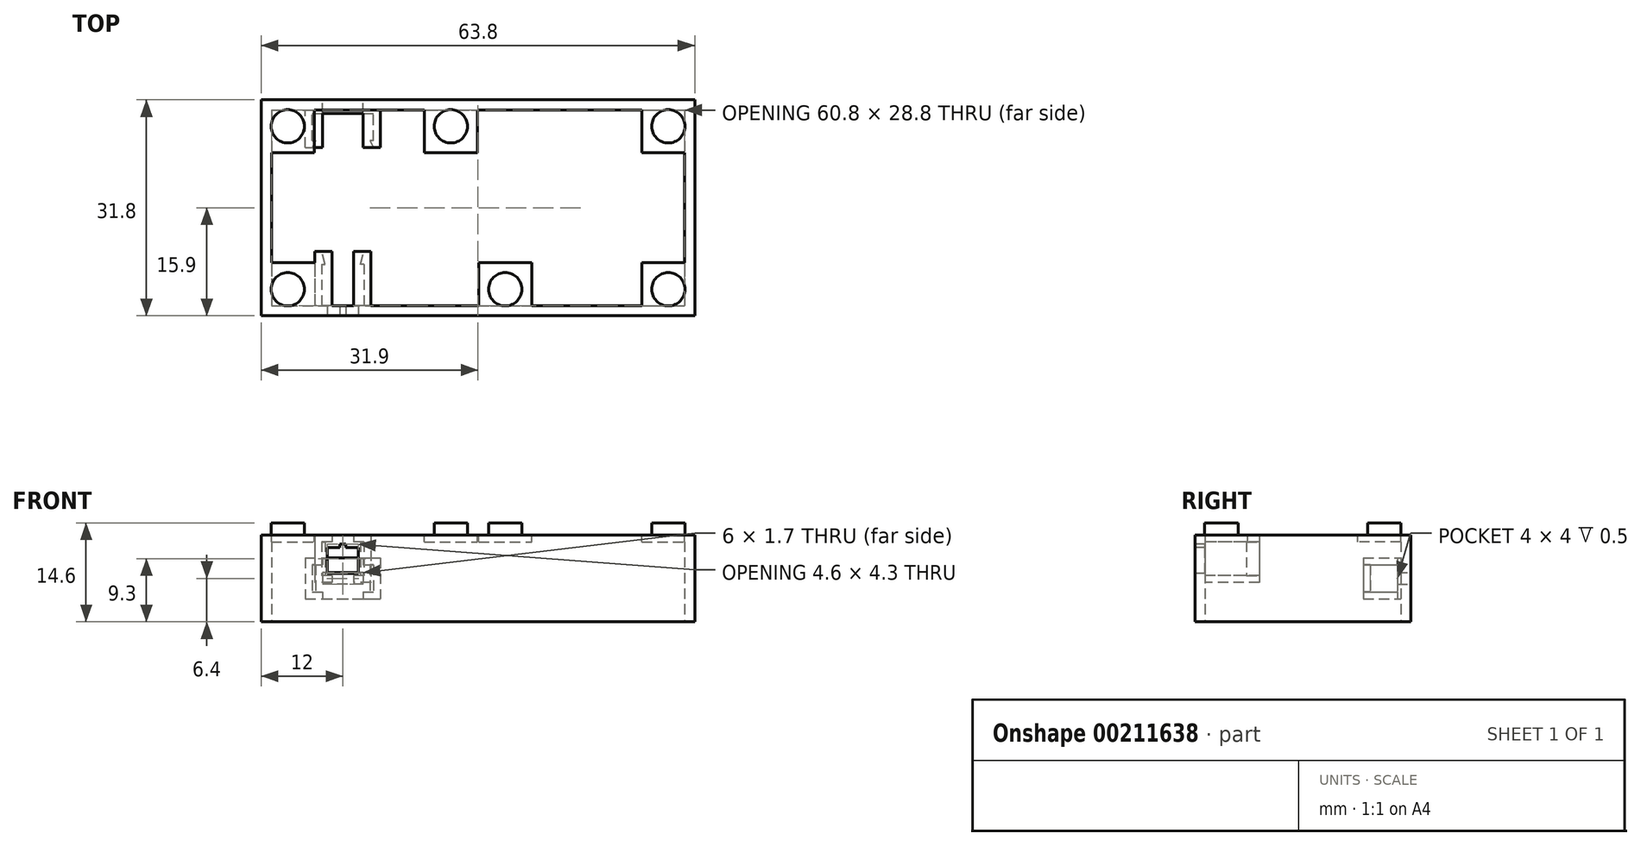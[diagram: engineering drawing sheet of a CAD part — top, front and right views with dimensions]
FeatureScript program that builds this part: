
annotation { "Feature Type Name" : "Feature", "Feature Type Description" : "" }
export const myFeature = defineFeature(function(context is Context, id is Id, definition is map)
    precondition{}
    {
        {
            var Q0;
            Q0=qCreatedBy(makeId("Top.planeOp"),FACE);
            var sketch = newSketch(context, id + "F0", { "sketchPlane" : qUnion([Q0])});
            skLineSegment(sketch, "E0.bottom", {"start": v(0, 31.8) * mm, "end": v(63.8, 31.8) * mm});
            skLineSegment(sketch, "E0.top", {"start": v(0, 0) * mm, "end": v(63.8, 0) * mm});
            skLineSegment(sketch, "E0.left", {"start": v(0, 31.8) * mm, "end": v(0, 0) * mm});
            skLineSegment(sketch, "E0.right", {"start": v(63.8, 31.8) * mm, "end": v(63.8, 0) * mm});
            skPoint(sketch, "E1", {"position": v(31.9, 31.8) * mm});
            skPoint(sketch, "E2", {"position": v(0, 15.9) * mm});
            skLineSegment(sketch, "E3.0", {"start": v(1.5, 30.3) * mm, "end": v(1.5, 1.5) * mm});
            skLineSegment(sketch, "E3.1", {"start": v(1.5, 30.3) * mm, "end": v(62.3, 30.3) * mm});
            skLineSegment(sketch, "E3.2", {"start": v(62.3, 30.3) * mm, "end": v(62.3, 1.5) * mm});
            skLineSegment(sketch, "E3.3", {"start": v(1.5, 1.5) * mm, "end": v(62.3, 1.5) * mm});
            skSolve(sketch);
        }
        {
            var Q0;
            Q0=qSketchRegion(id+"F0",true);
            extrude(context, id + "F1", {"entities" : qUnion([Q0]), "depth" : 12.8 * mm});
        }
        {
            var Q0;
            Q0=makeQuery(id+"F1.opExtrude","CAP_FACE",FACE,{"disambiguationData":[OSD([sQuery(id+"F0.wireOp",EDGE,"E0.bottom"),sQuery(id+"F0.wireOp",EDGE,"E0.top"),sQuery(id+"F0.wireOp",EDGE,"E0.left"),sQuery(id+"F0.wireOp",EDGE,"E0.right"),sQuery(id+"F0.wireOp",EDGE,"E3.0"),sQuery(id+"F0.wireOp",EDGE,"E3.1"),sQuery(id+"F0.wireOp",EDGE,"E3.2"),sQuery(id+"F0.wireOp",EDGE,"E3.3")])],"isStart":false});
            var sketch = newSketch(context, id + "F2", { "sketchPlane" : qUnion([Q0])});
            skLineSegment(sketch, "E4.bottom", {"start": v(0, 31.8) * mm, "end": v(7.8, 31.8) * mm});
            skLineSegment(sketch, "E4.top", {"start": v(0, 24) * mm, "end": v(7.8, 24) * mm});
            skLineSegment(sketch, "E4.left", {"start": v(0, 31.8) * mm, "end": v(0, 24) * mm});
            skLineSegment(sketch, "E4.right", {"start": v(7.8, 31.8) * mm, "end": v(7.8, 24) * mm});
            skLineSegment(sketch, "E5.bottom", {"start": v(0, 0) * mm, "end": v(7.8, 0) * mm});
            skLineSegment(sketch, "E5.top", {"start": v(0, 7.8) * mm, "end": v(7.8, 7.8) * mm});
            skLineSegment(sketch, "E5.left", {"start": v(0, 0) * mm, "end": v(0, 7.8) * mm});
            skLineSegment(sketch, "E5.right", {"start": v(7.8, 0) * mm, "end": v(7.8, 7.8) * mm});
            skLineSegment(sketch, "E6.bottom", {"start": v(63.8, 31.8) * mm, "end": v(56, 31.8) * mm});
            skLineSegment(sketch, "E6.top", {"start": v(63.8, 24) * mm, "end": v(56, 24) * mm});
            skLineSegment(sketch, "E6.left", {"start": v(63.8, 31.8) * mm, "end": v(63.8, 24) * mm});
            skLineSegment(sketch, "E6.right", {"start": v(56, 31.8) * mm, "end": v(56, 24) * mm});
            skLineSegment(sketch, "E7.bottom", {"start": v(63.8, 0) * mm, "end": v(56, 0) * mm});
            skLineSegment(sketch, "E7.top", {"start": v(63.8, 7.8) * mm, "end": v(56, 7.8) * mm});
            skLineSegment(sketch, "E7.left", {"start": v(63.8, 0) * mm, "end": v(63.8, 7.8) * mm});
            skLineSegment(sketch, "E7.right", {"start": v(56, 0) * mm, "end": v(56, 7.8) * mm});
            skPoint(sketch, "E8.centerSnap0", {"position": v(3.9, 24) * mm});
            skPoint(sketch, "E8.centerSnap1", {"position": v(0, 27.9) * mm});
            skPoint(sketch, "E9.centerSnap0", {"position": v(3.9, 0) * mm});
            skPoint(sketch, "E9.centerSnap1", {"position": v(0, 3.9) * mm});
            skPoint(sketch, "E10.centerSnap0", {"position": v(63.8, 27.9) * mm});
            skPoint(sketch, "E10.centerSnap1", {"position": v(59.9, 31.8) * mm});
            skPoint(sketch, "E11.centerSnap0", {"position": v(59.9, 0) * mm});
            skPoint(sketch, "E11.centerSnap1", {"position": v(63.8, 3.9) * mm});
            skLineSegment(sketch, "E12.bottom", {"start": v(24, 31.8) * mm, "end": v(31.8, 31.8) * mm});
            skLineSegment(sketch, "E12.top", {"start": v(24, 24) * mm, "end": v(31.8, 24) * mm});
            skLineSegment(sketch, "E12.left", {"start": v(24, 31.8) * mm, "end": v(24, 24) * mm});
            skLineSegment(sketch, "E12.right", {"start": v(31.8, 31.8) * mm, "end": v(31.8, 24) * mm});
            skLineSegment(sketch, "E13.bottom", {"start": v(39.8, 0) * mm, "end": v(32, 0) * mm});
            skLineSegment(sketch, "E13.top", {"start": v(39.8, 7.8) * mm, "end": v(32, 7.8) * mm});
            skLineSegment(sketch, "E13.left", {"start": v(39.8, 0) * mm, "end": v(39.8, 7.8) * mm});
            skLineSegment(sketch, "E13.right", {"start": v(32, 0) * mm, "end": v(32, 7.8) * mm});
            skPoint(sketch, "E14", {"position": v(27.9, 31.8) * mm});
            skPoint(sketch, "E15", {"position": v(35.9, 0) * mm});
            skSolve(sketch);
        }
        {
            var Q0;
            {var subQ0=sQuery(id+"F2.wireOp",EDGE,"E4.right");var subQ1=sQuery(id+"F2.wireOp",EDGE,"E4.top");var subQ2=makeQuery(id+"F2.imprint","INTERSECT",VERTEX,{"derivedFrom":[subQ1,subQ0]});Q0=makeQuery(id+"F2.imprint","IMPRINT",FACE,{"disambiguationData":[TD([[makeQuery(id+"F2.imprint","IMPRINT",EDGE,{"disambiguationData":[TD([[subQ2,1.0]])],"derivedFrom":subQ1}),1.0]])]});}
            var Q1;
            {var subQ0=sQuery(id+"F2.wireOp",EDGE,"E5.right");var subQ1=sQuery(id+"F2.wireOp",EDGE,"E5.top");var subQ2=makeQuery(id+"F2.imprint","INTERSECT",VERTEX,{"derivedFrom":[subQ1,subQ0]});Q1=makeQuery(id+"F2.imprint","IMPRINT",FACE,{"disambiguationData":[TD([[makeQuery(id+"F2.imprint","IMPRINT",EDGE,{"disambiguationData":[TD([[subQ2,1.0]])],"derivedFrom":subQ1}),-1.0]])]});}
            var Q2;
            {var subQ0=sQuery(id+"F2.wireOp",EDGE,"E7.right");var subQ1=sQuery(id+"F2.wireOp",EDGE,"E7.top");var subQ2=makeQuery(id+"F2.imprint","INTERSECT",VERTEX,{"derivedFrom":[subQ1,subQ0]});Q2=makeQuery(id+"F2.imprint","IMPRINT",FACE,{"disambiguationData":[TD([[makeQuery(id+"F2.imprint","IMPRINT",EDGE,{"disambiguationData":[TD([[subQ2,1.0]])],"derivedFrom":subQ1}),1.0]])]});}
            var Q3;
            {var subQ0=sQuery(id+"F2.wireOp",EDGE,"E6.right");var subQ1=sQuery(id+"F2.wireOp",EDGE,"E6.top");var subQ2=makeQuery(id+"F2.imprint","INTERSECT",VERTEX,{"derivedFrom":[subQ1,subQ0]});Q3=makeQuery(id+"F2.imprint","IMPRINT",FACE,{"disambiguationData":[TD([[makeQuery(id+"F2.imprint","IMPRINT",EDGE,{"disambiguationData":[TD([[subQ2,1.0]])],"derivedFrom":subQ1}),-1.0]])]});}
            var Q4;
            {var subQ0=sQuery(id+"F2.wireOp",EDGE,"E12.top");Q4=makeQuery(id+"F2.imprint","IMPRINT",FACE,{"disambiguationData":[TD([[makeQuery(id+"F2.imprint","IMPRINT",EDGE,{"derivedFrom":subQ0}),1.0]])]});}
            var Q5;
            {var subQ0=sQuery(id+"F2.wireOp",EDGE,"E13.top");Q5=makeQuery(id+"F2.imprint","IMPRINT",FACE,{"disambiguationData":[TD([[makeQuery(id+"F2.imprint","IMPRINT",EDGE,{"derivedFrom":subQ0}),1.0]])]});}
            extrude(context, id + "F3", {"entities" : qUnion([Q0, Q1, Q2, Q3, Q4, Q5]), "operationType" : NewBodyOperationType.ADD, "oppositeDirection" : true, "depth" : 1 * mm});
        }
        {
            var Q0;
            {var subQ0=sQuery(id+"F0.wireOp",EDGE,"E3.3");var subQ1=sQuery(id+"F0.wireOp",EDGE,"E3.2");var subQ2=sQuery(id+"F0.wireOp",EDGE,"E3.1");var subQ3=sQuery(id+"F0.wireOp",EDGE,"E3.0");Q0=makeQuery(id+"F3.boolean.opBoolean","MERGE",FACE,{"derivedFrom":[makeQuery(id+"F1.opExtrude","CAP_FACE",FACE,{"disambiguationData":[OSD([sQuery(id+"F0.wireOp",EDGE,"E0.bottom"),sQuery(id+"F0.wireOp",EDGE,"E0.top"),sQuery(id+"F0.wireOp",EDGE,"E0.left"),sQuery(id+"F0.wireOp",EDGE,"E0.right"),subQ3,subQ2,subQ1,subQ0])],"isStart":false}),makeQuery(id+"F3.opExtrude","CAP_FACE",FACE,{"disambiguationData":[OSD([subQ3,subQ2,sQuery(id+"F2.wireOp",EDGE,"E4.top"),sQuery(id+"F2.wireOp",EDGE,"E4.right")])],"isStart":true}),makeQuery(id+"F3.opExtrude","CAP_FACE",FACE,{"disambiguationData":[OSD([subQ3,subQ0,sQuery(id+"F2.wireOp",EDGE,"E5.top"),sQuery(id+"F2.wireOp",EDGE,"E5.right")])],"isStart":true}),makeQuery(id+"F3.opExtrude","CAP_FACE",FACE,{"disambiguationData":[OSD([subQ2,subQ1,sQuery(id+"F2.wireOp",EDGE,"E6.top"),sQuery(id+"F2.wireOp",EDGE,"E6.right")])],"isStart":true}),makeQuery(id+"F3.opExtrude","CAP_FACE",FACE,{"disambiguationData":[OSD([subQ1,subQ0,sQuery(id+"F2.wireOp",EDGE,"E7.top"),sQuery(id+"F2.wireOp",EDGE,"E7.right")])],"isStart":true})]});}
            var sketch = newSketch(context, id + "F4", { "sketchPlane" : qUnion([Q0])});
            skLineSegment(sketch, "E16.bottom", {"start": v(0, 31.8) * mm, "end": v(7.8, 31.8) * mm});
            skLineSegment(sketch, "E16.top", {"start": v(0, 24) * mm, "end": v(7.8, 24) * mm});
            skLineSegment(sketch, "E16.left", {"start": v(0, 31.8) * mm, "end": v(0, 24) * mm});
            skLineSegment(sketch, "E16.right", {"start": v(7.8, 31.8) * mm, "end": v(7.8, 24) * mm});
            skLineSegment(sketch, "E17.bottom", {"start": v(0, 0) * mm, "end": v(7.8, 0) * mm});
            skLineSegment(sketch, "E17.top", {"start": v(0, 7.8) * mm, "end": v(7.8, 7.8) * mm});
            skLineSegment(sketch, "E17.left", {"start": v(0, 0) * mm, "end": v(0, 7.8) * mm});
            skLineSegment(sketch, "E17.right", {"start": v(7.8, 0) * mm, "end": v(7.8, 7.8) * mm});
            skLineSegment(sketch, "E18.bottom", {"start": v(63.8, 31.8) * mm, "end": v(56, 31.8) * mm});
            skLineSegment(sketch, "E18.top", {"start": v(63.8, 24) * mm, "end": v(56, 24) * mm});
            skLineSegment(sketch, "E18.left", {"start": v(63.8, 31.8) * mm, "end": v(63.8, 24) * mm});
            skLineSegment(sketch, "E18.right", {"start": v(56, 31.8) * mm, "end": v(56, 24) * mm});
            skLineSegment(sketch, "E19.bottom", {"start": v(63.8, 0) * mm, "end": v(56, 0) * mm});
            skLineSegment(sketch, "E19.top", {"start": v(63.8, 7.8) * mm, "end": v(56, 7.8) * mm});
            skLineSegment(sketch, "E19.left", {"start": v(63.8, 0) * mm, "end": v(63.8, 7.8) * mm});
            skLineSegment(sketch, "E19.right", {"start": v(56, 0) * mm, "end": v(56, 7.8) * mm});
            skCircle(sketch, "E20", {"center": v(3.9, 27.9) * mm, "radius": 2.45 * mm});
            skPoint(sketch, "E20.centerSnap0", {"position": v(3.9, 31.8) * mm});
            skPoint(sketch, "E20.centerSnap1", {"position": v(0, 27.9) * mm});
            skCircle(sketch, "E21", {"center": v(3.9, 3.9) * mm, "radius": 2.45 * mm});
            skPoint(sketch, "E21.centerSnap0", {"position": v(3.9, 0) * mm});
            skPoint(sketch, "E21.centerSnap1", {"position": v(0, 3.9) * mm});
            skCircle(sketch, "E22", {"center": v(59.9, 27.9) * mm, "radius": 2.45 * mm});
            skPoint(sketch, "E22.centerSnap0", {"position": v(63.8, 27.9) * mm});
            skPoint(sketch, "E22.centerSnap1", {"position": v(59.9, 31.8) * mm});
            skCircle(sketch, "E23", {"center": v(59.9, 3.9) * mm, "radius": 2.45 * mm});
            skPoint(sketch, "E23.centerSnap0", {"position": v(59.9, 0) * mm});
            skPoint(sketch, "E23.centerSnap1", {"position": v(63.8, 3.9) * mm});
            skLineSegment(sketch, "E24.bottom", {"start": v(31.8, 24) * mm, "end": v(24, 24) * mm});
            skLineSegment(sketch, "E24.top", {"start": v(31.8, 31.8) * mm, "end": v(24, 31.8) * mm});
            skLineSegment(sketch, "E24.left", {"start": v(31.8, 24) * mm, "end": v(31.8, 31.8) * mm});
            skLineSegment(sketch, "E24.right", {"start": v(24, 24) * mm, "end": v(24, 31.8) * mm});
            skLineSegment(sketch, "E25.bottom", {"start": v(32, 7.8) * mm, "end": v(39.8, 7.8) * mm});
            skLineSegment(sketch, "E25.top", {"start": v(32, 0) * mm, "end": v(39.8, 0) * mm});
            skLineSegment(sketch, "E25.left", {"start": v(32, 7.8) * mm, "end": v(32, 0) * mm});
            skLineSegment(sketch, "E25.right", {"start": v(39.8, 7.8) * mm, "end": v(39.8, 0) * mm});
            skPoint(sketch, "E26", {"position": v(27.9, 31.8) * mm});
            skPoint(sketch, "E27", {"position": v(24, 27.9) * mm});
            skPoint(sketch, "E28", {"position": v(35.9, 7.8) * mm});
            skPoint(sketch, "E29", {"position": v(32, 3.9) * mm});
            skCircle(sketch, "E30", {"center": v(27.9, 27.9) * mm, "radius": 2.45 * mm});
            skCircle(sketch, "E31", {"center": v(35.9, 3.9) * mm, "radius": 2.45 * mm});
            skSolve(sketch);
        }
        {
            var Q0;
            Q0=makeQuery(id+"F4.imprint","IMPRINT",FACE,{"disambiguationData":[TD([[makeQuery(id+"F4.imprint","IMPRINT",EDGE,{"derivedFrom":sQuery(id+"F4.wireOp",EDGE,"E20")}),1.0]])]});
            var Q1;
            Q1=makeQuery(id+"F4.imprint","IMPRINT",FACE,{"disambiguationData":[TD([[makeQuery(id+"F4.imprint","IMPRINT",EDGE,{"derivedFrom":sQuery(id+"F4.wireOp",EDGE,"E22")}),1.0]])]});
            var Q2;
            Q2=makeQuery(id+"F4.imprint","IMPRINT",FACE,{"disambiguationData":[TD([[makeQuery(id+"F4.imprint","IMPRINT",EDGE,{"derivedFrom":sQuery(id+"F4.wireOp",EDGE,"E23")}),1.0]])]});
            var Q3;
            Q3=makeQuery(id+"F4.imprint","IMPRINT",FACE,{"disambiguationData":[TD([[makeQuery(id+"F4.imprint","IMPRINT",EDGE,{"derivedFrom":sQuery(id+"F4.wireOp",EDGE,"E21")}),1.0]])]});
            var Q4;
            Q4=makeQuery(id+"F4.imprint","IMPRINT",FACE,{"disambiguationData":[TD([[makeQuery(id+"F4.imprint","IMPRINT",EDGE,{"derivedFrom":sQuery(id+"F4.wireOp",EDGE,"E30")}),1.0]])]});
            var Q5;
            Q5=makeQuery(id+"F4.imprint","IMPRINT",FACE,{"disambiguationData":[TD([[makeQuery(id+"F4.imprint","IMPRINT",EDGE,{"derivedFrom":sQuery(id+"F4.wireOp",EDGE,"E31")}),1.0]])]});
            extrude(context, id + "F5", {"entities" : qUnion([Q0, Q1, Q2, Q3, Q4, Q5]), "operationType" : NewBodyOperationType.ADD, "depth" : 1.8 * mm});
        }
        {
            var Q0;
            Q0=makeQuery(id+"F1.opExtrude","SWEPT_FACE",FACE,{"disambiguationData":[OSD([sQuery(id+"F0.wireOp",EDGE,"E0.top")])]});
            var sketch = newSketch(context, id + "F6", { "sketchPlane" : qUnion([Q0])});
            skLineSegment(sketch, "E32.bottom", {"start": v(9.7, 10.95) * mm, "end": v(14.3, 10.95) * mm});
            skLineSegment(sketch, "E32.top", {"start": v(9.7, 7.15) * mm, "end": v(14.3, 7.15) * mm});
            skLineSegment(sketch, "E32.left", {"start": v(9.7, 10.95) * mm, "end": v(9.7, 7.15) * mm});
            skLineSegment(sketch, "E32.right", {"start": v(14.3, 10.95) * mm, "end": v(14.3, 7.15) * mm});
            skPoint(sketch, "E33", {"position": v(12, 12.8) * mm});
            skPoint(sketch, "E34", {"position": v(12, 10.95) * mm});
            skLineSegment(sketch, "E35.bottom", {"start": v(11.58, 11.45) * mm, "end": v(12.42, 11.45) * mm});
            skLineSegment(sketch, "E35.top", {"start": v(11.58, 10.95) * mm, "end": v(12.42, 10.95) * mm});
            skLineSegment(sketch, "E35.left", {"start": v(11.58, 11.45) * mm, "end": v(11.58, 10.95) * mm});
            skLineSegment(sketch, "E35.right", {"start": v(12.43, 11.45) * mm, "end": v(12.43, 10.95) * mm});
            skLineSegment(sketch, "E36", {"start": v(12, 11.8) * mm, "end": v(12, 6.8) * mm, "construction": true});
            skPoint(sketch, "E37", {"position": v(12, 9.3) * mm});
            skLineSegment(sketch, "E38", {"start": v(12, 11.45) * mm, "end": v(12, 7.15) * mm, "construction": true});
            skSolve(sketch);
        }
        {
            var Q0;
            Q0=makeQuery(id+"F6.imprint","IMPRINT",FACE,{"disambiguationData":[TD([[makeQuery(id+"F6.imprint","IMPRINT",EDGE,{"derivedFrom":sQuery(id+"F6.wireOp",EDGE,"E32.bottom")}),-1.0]])]});
            var Q1;
            Q1=makeQuery(id+"F6.imprint","IMPRINT",FACE,{"disambiguationData":[TD([[makeQuery(id+"F6.imprint","IMPRINT",EDGE,{"derivedFrom":sQuery(id+"F6.wireOp",EDGE,"b1744aed-7852-425b-a269-eb57eedebe04.bottom")}),-1.0]])]});
            var Q2;
            Q2=makeQuery(id+"F6.imprint","IMPRINT",FACE,{"disambiguationData":[TD([[makeQuery(id+"F6.imprint","IMPRINT",EDGE,{"derivedFrom":sQuery(id+"F6.wireOp",EDGE,"E35.bottom")}),-1.0]])]});
            extrude(context, id + "F7", {"entities" : qUnion([Q0, Q1, Q2]), "operationType" : NewBodyOperationType.REMOVE, "oppositeDirection" : true, "depth" : 25.4 * mm});
        }
        {
            var Q0;
            Q0=makeQuery(id+"F1.opExtrude","SWEPT_FACE",FACE,{"disambiguationData":[OSD([sQuery(id+"F0.wireOp",EDGE,"E3.3")])]});
            var sketch = newSketch(context, id + "F8", { "sketchPlane" : qUnion([Q0])});
            skLineSegment(sketch, "E39.0", {"start": v(-14.3, 7.15) * mm, "end": v(-14.3, 10.95) * mm});
            skLineSegment(sketch, "E40.0", {"start": v(-14.3, 10.95) * mm, "end": v(-12.43, 10.95) * mm});
            skLineSegment(sketch, "E41.0", {"start": v(-12.43, 10.95) * mm, "end": v(-12.43, 11.45) * mm});
            skPoint(sketch, "E42.0", {"position": v(-12, 11.45) * mm});
            skLineSegment(sketch, "E43.0", {"start": v(-12.43, 11.45) * mm, "end": v(-11.58, 11.45) * mm});
            skLineSegment(sketch, "E44.0", {"start": v(-11.58, 10.95) * mm, "end": v(-11.58, 11.45) * mm});
            skLineSegment(sketch, "E45.0", {"start": v(-11.58, 10.95) * mm, "end": v(-9.7, 10.95) * mm});
            skLineSegment(sketch, "E46.0", {"start": v(-9.7, 7.15) * mm, "end": v(-9.7, 10.95) * mm});
            skLineSegment(sketch, "E47.0", {"start": v(-14.3, 7.15) * mm, "end": v(-9.7, 7.15) * mm});
            skLineSegment(sketch, "E48.bottom", {"start": v(-15.1, 11.8) * mm, "end": v(-8.9, 11.8) * mm});
            skLineSegment(sketch, "E48.top", {"start": v(-15.1, 6.8) * mm, "end": v(-8.9, 6.8) * mm});
            skLineSegment(sketch, "E48.left", {"start": v(-15.1, 11.8) * mm, "end": v(-15.1, 6.8) * mm});
            skLineSegment(sketch, "E48.right", {"start": v(-8.9, 11.8) * mm, "end": v(-8.9, 6.8) * mm});
            skPoint(sketch, "E49", {"position": v(-12, 7.15) * mm});
            skPoint(sketch, "E50", {"position": v(-12, 6.8) * mm});
            skLineSegment(sketch, "E51", {"start": v(-12, 11.45) * mm, "end": v(-12, 7.15) * mm, "construction": true});
            skPoint(sketch, "E52", {"position": v(-12, 9.3) * mm});
            skPoint(sketch, "E53", {"position": v(-8.9, 9.3) * mm});
            skLineSegment(sketch, "E54.0", {"start": v(-16.1, 12.8) * mm, "end": v(-7.9, 12.8) * mm});
            skLineSegment(sketch, "E54.1", {"start": v(-16.1, 12.8) * mm, "end": v(-16.1, 5.8) * mm});
            skLineSegment(sketch, "E54.2", {"start": v(-16.1, 5.8) * mm, "end": v(-7.9, 5.8) * mm});
            skLineSegment(sketch, "E54.3", {"start": v(-7.9, 12.8) * mm, "end": v(-7.9, 5.8) * mm});
            skLineSegment(sketch, "E55.bottom", {"start": v(-16.1, 12.8) * mm, "end": v(-13.6, 12.8) * mm});
            skLineSegment(sketch, "E55.top", {"start": v(-16.1, 5.8) * mm, "end": v(-13.6, 5.8) * mm});
            skLineSegment(sketch, "E55.right", {"start": v(-13.6, 12.8) * mm, "end": v(-13.6, 5.8) * mm});
            skLineSegment(sketch, "E56.bottom", {"start": v(-7.9, 12.8) * mm, "end": v(-10.4, 12.8) * mm});
            skLineSegment(sketch, "E56.top", {"start": v(-7.9, 5.8) * mm, "end": v(-10.4, 5.8) * mm});
            skLineSegment(sketch, "E56.right", {"start": v(-10.4, 12.8) * mm, "end": v(-10.4, 5.8) * mm});
            skSolve(sketch);
        }
        {
            var Q0;
            {var subQ1=sQuery(id+"F8.wireOp",EDGE,"E48.left");Q0=makeQuery(id+"F8.imprint","IMPRINT",FACE,{"disambiguationData":[TD([[makeQuery(id+"F8.imprint","IMPRINT",EDGE,{"derivedFrom":subQ1}),-1.0]])]});}
            var Q1;
            {var subQ0=sQuery(id+"F8.wireOp",EDGE,"E48.right");Q1=makeQuery(id+"F8.imprint","IMPRINT",FACE,{"disambiguationData":[TD([[makeQuery(id+"F8.imprint","IMPRINT",EDGE,{"derivedFrom":subQ0}),1.0]])]});}
            extrude(context, id + "F9", {"entities" : qUnion([Q0, Q1]), "operationType" : NewBodyOperationType.ADD, "depth" : 8 * mm});
        }
        {
            var Q0;
            {var subQ0=sQuery(id+"F8.wireOp",EDGE,"E48.top");Q0=makeQuery(id+"F9.opExtrude","SWEPT_FACE",FACE,{"disambiguationData":[OSD([subQ0]),TDD([makeQuery(id+"F8.imprint","IMPRINT",EDGE,{"disambiguationData":[TD([[makeQuery(id+"F8.imprint","INTERSECT",VERTEX,{"derivedFrom":[subQ0,sQuery(id+"F8.wireOp",EDGE,"E48.left")]}),-1.0]])],"derivedFrom":subQ0})])]});}
            var sketch = newSketch(context, id + "F10", { "sketchPlane" : qUnion([Q0])});
            skLineSegment(sketch, "E57", {"start": v(15.1, 7.6) * mm, "end": v(14.6, 7.6) * mm});
            skLineSegment(sketch, "E58", {"start": v(14.6, 7.6) * mm, "end": v(15.1, 9.5) * mm});
            skLineSegment(sketch, "E59.0", {"start": v(8.9, 9.5) * mm, "end": v(8.9, 1.5) * mm});
            skLineSegment(sketch, "E60", {"start": v(8.9, 7.6) * mm, "end": v(9.4, 7.6) * mm});
            skLineSegment(sketch, "E61", {"start": v(9.4, 7.6) * mm, "end": v(8.9, 9.5) * mm});
            skSolve(sketch);
        }
        {
            var Q0;
            {var subQ0=sQuery(id+"F10.wireOp",EDGE,"E57");Q0=makeQuery(id+"F10.imprint","IMPRINT",FACE,{"disambiguationData":[TD([[makeQuery(id+"F10.imprint","IMPRINT",EDGE,{"derivedFrom":subQ0}),-1.0]])]});}
            var Q1;
            {var subQ2=sQuery(id+"F10.wireOp",EDGE,"E60");Q1=makeQuery(id+"F10.imprint","IMPRINT",FACE,{"disambiguationData":[TD([[makeQuery(id+"F10.imprint","IMPRINT",EDGE,{"derivedFrom":subQ2}),1.0]])]});}
            extrude(context, id + "F11", {"entities" : qUnion([Q0, Q1]), "operationType" : NewBodyOperationType.ADD, "endBound" : BoundingType.UP_TO_NEXT, "depth" : 25.4 * mm});
        }
        {
            var Q0;
            Q0=makeQuery(id+"F1.opExtrude","SWEPT_FACE",FACE,{"disambiguationData":[OSD([sQuery(id+"F0.wireOp",EDGE,"E3.3")])]});
            var sketch = newSketch(context, id + "F12", { "sketchPlane" : qUnion([Q0])});
            skLineSegment(sketch, "E62.bottom", {"start": v(-7.9, 12.8) * mm, "end": v(-4.9, 12.8) * mm});
            skLineSegment(sketch, "E62.top", {"start": v(-7.9, 11.8) * mm, "end": v(-4.9, 11.8) * mm});
            skLineSegment(sketch, "E62.left", {"start": v(-7.9, 12.8) * mm, "end": v(-7.9, 11.8) * mm});
            skLineSegment(sketch, "E62.right", {"start": v(-4.9, 12.8) * mm, "end": v(-4.9, 11.8) * mm});
            skSolve(sketch);
        }
        {
            var Q0;
            {var subQ2=sQuery(id+"F12.wireOp",EDGE,"E62.left");Q0=makeQuery(id+"F12.imprint","IMPRINT",FACE,{"disambiguationData":[TD([[makeQuery(id+"F12.imprint","IMPRINT",EDGE,{"derivedFrom":subQ2}),1.0]])]});}
            var Q1;
            Q1=makeQuery(id+"F3.opExtrude","SWEPT_FACE",FACE,{"disambiguationData":[OSD([sQuery(id+"F2.wireOp",EDGE,"E5.top")])]});
            extrude(context, id + "F13", {"entities" : qUnion([Q0]), "operationType" : NewBodyOperationType.ADD, "endBound" : BoundingType.UP_TO_SURFACE, "endBoundEntityFace" : qUnion([Q1]), "depth" : 25.4 * mm});
        }
        {
            var Q0;
            Q0=makeQuery(id+"F1.opExtrude","SWEPT_FACE",FACE,{"disambiguationData":[OSD([sQuery(id+"F0.wireOp",EDGE,"E0.bottom")])]});
            var sketch = newSketch(context, id + "F14", { "sketchPlane" : qUnion([Q0])});
            skLineSegment(sketch, "E63.bottom", {"start": v(-15, 7.25) * mm, "end": v(-9, 7.25) * mm});
            skLineSegment(sketch, "E63.top", {"start": v(-15, 5.55) * mm, "end": v(-9, 5.55) * mm});
            skLineSegment(sketch, "E63.left", {"start": v(-15, 7.25) * mm, "end": v(-15, 5.55) * mm});
            skLineSegment(sketch, "E63.right", {"start": v(-9, 7.25) * mm, "end": v(-9, 5.55) * mm});
            skPoint(sketch, "E64", {"position": v(0, 6.4) * mm});
            skPoint(sketch, "E65", {"position": v(-9, 6.4) * mm});
            skPoint(sketch, "E66", {"position": v(-12, 7.25) * mm});
            skSolve(sketch);
        }
        {
            var Q0;
            Q0=makeQuery(id+"F14.imprint","IMPRINT",FACE,{"disambiguationData":[TD([[makeQuery(id+"F14.imprint","IMPRINT",EDGE,{"derivedFrom":sQuery(id+"F14.wireOp",EDGE,"E63.bottom")}),-1.0]])]});
            extrude(context, id + "F15", {"entities" : qUnion([Q0]), "operationType" : NewBodyOperationType.REMOVE, "oppositeDirection" : true, "depth" : 2.54 * mm});
        }
        {
            var Q0;
            Q0=makeQuery(id+"F1.opExtrude","SWEPT_FACE",FACE,{"disambiguationData":[OSD([sQuery(id+"F0.wireOp",EDGE,"E3.1")])]});
            var sketch = newSketch(context, id + "F16", { "sketchPlane" : qUnion([Q0])});
            skLineSegment(sketch, "E67.bottom", {"start": v(6.5, 9.4) * mm, "end": v(17.5, 9.4) * mm});
            skLineSegment(sketch, "E67.top", {"start": v(6.5, 3.4) * mm, "end": v(17.5, 3.4) * mm});
            skLineSegment(sketch, "E67.left", {"start": v(6.5, 9.4) * mm, "end": v(6.5, 3.4) * mm});
            skLineSegment(sketch, "E67.right", {"start": v(17.5, 9.4) * mm, "end": v(17.5, 3.4) * mm});
            skPoint(sketch, "E68", {"position": v(12, 9.4) * mm});
            skPoint(sketch, "E69", {"position": v(12, 7.25) * mm});
            skPoint(sketch, "E70", {"position": v(15, 6.4) * mm});
            skPoint(sketch, "E71", {"position": v(17.5, 6.4) * mm});
            skSolve(sketch);
        }
        {
            var Q0;
            Q0=makeQuery(id+"F16.imprint","IMPRINT",FACE,{"disambiguationData":[TD([[makeQuery(id+"F16.imprint","IMPRINT",EDGE,{"derivedFrom":sQuery(id+"F16.wireOp",EDGE,"E67.bottom")}),-1.0]])]});
            extrude(context, id + "F17", {"entities" : qUnion([Q0]), "operationType" : NewBodyOperationType.ADD, "depth" : .5 * mm});
        }
        {
            var Q0;
            Q0=makeQuery(id+"F17.opExtrude","CAP_FACE",FACE,{"disambiguationData":[OSD([sQuery(id+"F0.wireOp",EDGE,"E3.1"),sQuery(id+"F14.wireOp",EDGE,"E63.bottom"),sQuery(id+"F14.wireOp",EDGE,"E63.top"),sQuery(id+"F14.wireOp",EDGE,"E63.left"),sQuery(id+"F14.wireOp",EDGE,"E63.right"),sQuery(id+"F16.wireOp",EDGE,"E67.bottom"),sQuery(id+"F16.wireOp",EDGE,"E67.top"),sQuery(id+"F16.wireOp",EDGE,"E67.left"),sQuery(id+"F16.wireOp",EDGE,"E67.right")])],"isStart":false});
            var sketch = newSketch(context, id + "F18", { "sketchPlane" : qUnion([Q0])});
            skLineSegment(sketch, "E72.0", {"start": v(6.5, 9.4) * mm, "end": v(6.5, 3.4) * mm});
            skLineSegment(sketch, "E72.1", {"start": v(6.5, 9.4) * mm, "end": v(17.5, 9.4) * mm});
            skLineSegment(sketch, "E72.2", {"start": v(17.5, 9.4) * mm, "end": v(17.5, 3.4) * mm});
            skLineSegment(sketch, "E72.3", {"start": v(6.5, 3.4) * mm, "end": v(17.5, 3.4) * mm});
            skLineSegment(sketch, "E73.bottom", {"start": v(7.5, 8.4) * mm, "end": v(16.5, 8.4) * mm});
            skLineSegment(sketch, "E73.top", {"start": v(7.5, 4.4) * mm, "end": v(16.5, 4.4) * mm});
            skLineSegment(sketch, "E73.left", {"start": v(7.5, 8.4) * mm, "end": v(7.5, 4.4) * mm});
            skLineSegment(sketch, "E73.right", {"start": v(16.5, 8.4) * mm, "end": v(16.5, 4.4) * mm});
            skPoint(sketch, "E74", {"position": v(12, 8.4) * mm});
            skPoint(sketch, "E75", {"position": v(12, 9.4) * mm});
            skPoint(sketch, "E76", {"position": v(16.5, 6.4) * mm});
            skPoint(sketch, "E77", {"position": v(17.5, 6.4) * mm});
            skLineSegment(sketch, "E78.bottom", {"start": v(17.5, 9.4) * mm, "end": v(15, 9.4) * mm});
            skLineSegment(sketch, "E78.top", {"start": v(17.5, 3.4) * mm, "end": v(15, 3.4) * mm});
            skLineSegment(sketch, "E78.right", {"start": v(15, 9.4) * mm, "end": v(15, 3.4) * mm});
            skLineSegment(sketch, "E79.bottom", {"start": v(6.5, 9.4) * mm, "end": v(9, 9.4) * mm});
            skLineSegment(sketch, "E79.top", {"start": v(6.5, 3.4) * mm, "end": v(9, 3.4) * mm});
            skLineSegment(sketch, "E79.right", {"start": v(9, 9.4) * mm, "end": v(9, 3.4) * mm});
            skSolve(sketch);
        }
        {
            var Q0;
            {var subQ1=sQuery(id+"F18.wireOp",EDGE,"E73.left");Q0=makeQuery(id+"F18.imprint","IMPRINT",FACE,{"disambiguationData":[TD([[makeQuery(id+"F18.imprint","IMPRINT",EDGE,{"derivedFrom":subQ1}),-1.0]])]});}
            var Q1;
            {var subQ1=sQuery(id+"F18.wireOp",EDGE,"E73.right");Q1=makeQuery(id+"F18.imprint","IMPRINT",FACE,{"disambiguationData":[TD([[makeQuery(id+"F18.imprint","IMPRINT",EDGE,{"derivedFrom":subQ1}),1.0]])]});}
            extrude(context, id + "F19", {"entities" : qUnion([Q0, Q1]), "operationType" : NewBodyOperationType.ADD, "depth" : 5 * mm});
        }
        {
            var Q0;
            {var subQ0=sQuery(id+"F18.wireOp",EDGE,"E73.top");Q0=makeQuery(id+"F19.opExtrude","SWEPT_FACE",FACE,{"disambiguationData":[OSD([subQ0]),TDD([makeQuery(id+"F18.imprint","IMPRINT",EDGE,{"disambiguationData":[TD([[makeQuery(id+"F18.imprint","INTERSECT",VERTEX,{"derivedFrom":[subQ0,sQuery(id+"F18.wireOp",EDGE,"E73.left")]}),-1.0]])],"derivedFrom":subQ0})])]});}
            var sketch = newSketch(context, id + "F20", { "sketchPlane" : qUnion([Q0])});
            skLineSegment(sketch, "E80.0", {"start": v(7.5, 24.8) * mm, "end": v(7.5, 29.8) * mm});
            skLineSegment(sketch, "E80.1", {"start": v(16.5, 24.8) * mm, "end": v(16.5, 29.8) * mm});
            skLineSegment(sketch, "E81", {"start": v(16.5, 25.8) * mm, "end": v(16, 25.8) * mm});
            skLineSegment(sketch, "E82", {"start": v(16, 25.8) * mm, "end": v(16.5, 24.8) * mm});
            skLineSegment(sketch, "E83", {"start": v(7.5, 25.8) * mm, "end": v(8, 25.8) * mm});
            skLineSegment(sketch, "E84", {"start": v(8, 25.8) * mm, "end": v(7.5, 24.8) * mm});
            skSolve(sketch);
        }
        {
            var Q0;
            {var subQ3=sQuery(id+"F20.wireOp",EDGE,"E83");Q0=makeQuery(id+"F20.imprint","IMPRINT",FACE,{"disambiguationData":[TD([[makeQuery(id+"F20.imprint","IMPRINT",EDGE,{"derivedFrom":subQ3}),-1.0]])]});}
            var Q1;
            {var subQ2=sQuery(id+"F20.wireOp",EDGE,"E81");Q1=makeQuery(id+"F20.imprint","IMPRINT",FACE,{"disambiguationData":[TD([[makeQuery(id+"F20.imprint","IMPRINT",EDGE,{"derivedFrom":subQ2}),1.0]])]});}
            extrude(context, id + "F21", {"entities" : qUnion([Q0, Q1]), "operationType" : NewBodyOperationType.ADD, "endBound" : BoundingType.UP_TO_NEXT, "depth" : 25.4 * mm});
        }
    });
